# Revit family: Domotics-DomesticRanges-GEWISS-CHORUS_COMMAND-INTERMEDIATE_SWITCH_FAST_WIRING_2M
name_source: partatom
category: Apparecchi elettrici
revit_build: Autodesk Revit 2016 (Build: 20161004_0715(x64)
units: mm (PartAtom-declared; Revit-internal decimal feet)

## family parameters
Condiviso = Sì
Host = Superficie
Mantenere orientamento annotazione = Sì
Numero OmniClass = 23.80.50.11.14
Punto di calcolo locali = No
Quota connettore circolare = Usa diametro
Taglio con vuoti quando caricato = Sì
Tipo di parte = Normale
Titolo OmniClass = Switches

## types (9) — shared parameters
Bidimensionale = bidimensionale invertitori 2m : GW12103
Breaking capacity = 1.25 In (200 position changes)
Breaking capacity: = 1.25 In (200 position changes)
Carico apparente = 0 VA
Catalogue = DOMOTICS
Catalogue Range = CHORUS - DOMESTIC RANGE
Category = Reversing switch
Electrocod = 0130
Glow Wire Test = 850°C
IDF = a49b593c-ff32-4dd4-849a-cbafabc949ea
IDT = 45b86141-2549-4b1d-b268-6b8eb2f32dad
Immagine tipo = GW14103.jpg
Insulation resistance = > 5 MOhm
Larghezza pulsante = 46 mm  [stored 0.150919 ft]
N. poli = 1
No. Chorus modules = 2
Produttore = GEWISS S.p.A.
Prolonged operation (no.of position changes) = 40.000 at In 250 V ac cosÃ˜=0,6
Prospetto di default = 1219 mm
Resistance at test voltage = 2000 V at 50 Hz for 1 minute
SEO = Intermediate switch
Simbolo = SIMBOLO INVERTITORI : INV1PLUM
Standard = EN 60669-1
Standard; = EN 60669-1
Technical sheet = https://www.gewiss.com
Terminal grip on cable traction = > 50 N
Terminal tightening capacity = min. 0,75 - max. 2x4
Terminal tightening capacity flexible cables (mm2) = min. 0,75 - max. 2x4
Terminal tightening capacity rigid cables (mm2) = min. 0,5 - max. 2x2,5
Thermo-pressure with ball = 125
Tipo_ = CHORUS INVERTITORI 2M_BASE : GW14103 - Titanio - Illuminabile segnalazione
URL = https://www.gewiss.com
Version file RFA = 19.0
Volt = 230 V
Voltage = 250 V ac
Voltage: = 250 V ac
Wiring terminals = Quick, with spring

## per-type parameters (varying)
| type | Button key | Colour | Description: | Descrizione | EAN code | Modello | Type |
| GW14101F - Intermediate switch 2M 1P 16AX fast wiring Titanium | Neutral | Titanium | 1P - 16AX | REV.SWITCH 2M 1P 16AX R.W. TITANIUM | 8011564265745 | GW14101F | General |
| GW12102F - Intermediate switch 2M 1P 16AX illuminable fast wiring Black | With diffuser | Black | 1P - 16AX illuminable | REV.SWITCH 2M 1P 16AX ILL LOC R.W. BLACK | 8011564268784 | GW12102F | Backlit |
| GW12101F - Intermediate switch 2M 1P 16AX fast wiring Black | Neutral | Black | 1P - 16AX | REV.SWITCH 2M 1P 16AX R.WIRING BLACK | 8011564268746 | GW12101F | General |
| GW14102F - Intermediate switch 2M 1P 16AX illuminable fast wiring Titanium | With diffuser | Titanium | 1P - 16AX illuminable | REV.SWITCH 2M 1P 16AX ILL LOC R.W. T | 8011564265769 | GW14102F | Backlit |
| GW12103F - Intermediate switch 2M 1P 16AX illuminable fast wiring Black | With replaceable neutral lens | Black | 1P - 16AX illuminable | REV.SWITCH 2M 1P 16AX ILL SIG R.W. BLACK | 8011564268814 | GW12103F | Indicator |
| GW10103F - Intermediate switch 2M 1P 16AX illuminable fast wiring White | With replaceable neutral lens | White | 1P - 16AX illuminable | REV.SWITCH 2M 1P 16AX ILL SIG R.W. WHITE | 8011564259997 | GW10103F | Indicator |
| GW10102F - Intermediate switch 2M 1P 16AX illuminable fast wiring White | With diffuser | White | 1P - 16AX illuminable | REV-SWITCH 2M 1P 16AX ILL LOC R.W. WHITE | 8011564259973 | GW10102F | Backlit |
| GW10101F - Intermediate switch 2M 1P 16AX fast wiring White | Neutral | White | 1P - 16AX | REV.SWITCH, 2M 1P 16AX R.W. WHITE | 8011564259959 | GW10101F | General |
| GW14103F - Intermediate switch 2M 1P 16AX illuminable fast wiring Titanium | With replaceable neutral lens | Titanium | 1P - 16AX illuminable | REV.SWITCH 2M 1P 16AX ILL SIG R.W. T | 8011564265783 | GW14103F | Indicator |

note: source unit labels omitted for Thermo-pressure with ball — the stored unit's dimension contradicts the parameter name (converter mislabeling)

note: [stored X ft] marks values corroborated as IEEE doubles in the binary element streams (Revit-internal decimal feet)

## geometry (parser evidence)
native form markers: Sweep x2
no freeform markers — native parametric forms only
